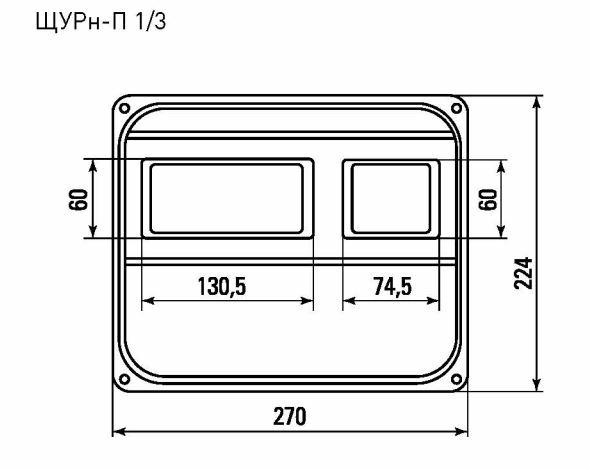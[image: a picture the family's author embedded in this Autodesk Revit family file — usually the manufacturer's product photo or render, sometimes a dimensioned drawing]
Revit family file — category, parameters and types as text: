
# Revit family: EKF_EE_Короб_ВерхНиз_КСС-КЭТ(700х300х150)_Basic
name_source: partatom
category: Электрооборудование
units: mm (PartAtom-declared; Revit-internal decimal feet)

## family parameters
Всегда вертикально = Да
На основе рабочей плоскости = Нет
Общий = Нет
При загрузке вырезать с полостями = Нет
Размер круглого соединителя = Использовать диаметр
Тип детали = Силовой щит
Точка расчета площади = Да

## types (1)
- Короб верх/низ для КСС/КЭТ (700х300х150) EKF Basic
    ADSK_Единица измерения = компл.
    ADSK_Завод-изготовитель = EKF
    ADSK_Классификация нагрузок = Прочее
    ADSK_Код изделия = uerm2-kor-700-bas
    ADSK_Количество = 1
    ADSK_Количество фаз = 3
    ADSK_Коэффициент мощности = 1
    ADSK_Марка = Короб верх/низ для КСС/КЭТ
    ADSK_Масса = 0
    ADSK_Материал = RAL 7035_Сталь
    ADSK_Наименование = Короб верх/низ для КСС/КЭТ (700х300х150) EKF BasicКороб верх/низ для КСС/КЭТ (700х300х150) EKF Basic
    ADSK_Напряжение = 400 В
    ADSK_Номинальная мощность = 0 Вт
    ADSK_Обозначение = Короб верх/низ для КСС/КЭТ
    ADSK_Полная мощность = 0 В·А
    ADSK_Размер_Высота = 700 мм
    ADSK_Размер_Глубина = 150 мм
    ADSK_Размер_Ширина = 300 мм
    ADSK_Ток = 125 А
    Изготовитель = EKF
    Количество DIN-реек = 0
    Количество модулей на DIN-рейке = 0
    Максимальное количество модулей = 0
    Описание = Короб верх/низ для КСС/КЭТ (700х300х150) EKF BasicКороб верх/низ для КСС/КЭТ (700х300х150) EKF Basic
    Серия номенклатуры = Basic
    Степень защиты IP = IP31
    ТВ = EKF
    Тип = 213 мм
    Тип установки = Навесной
